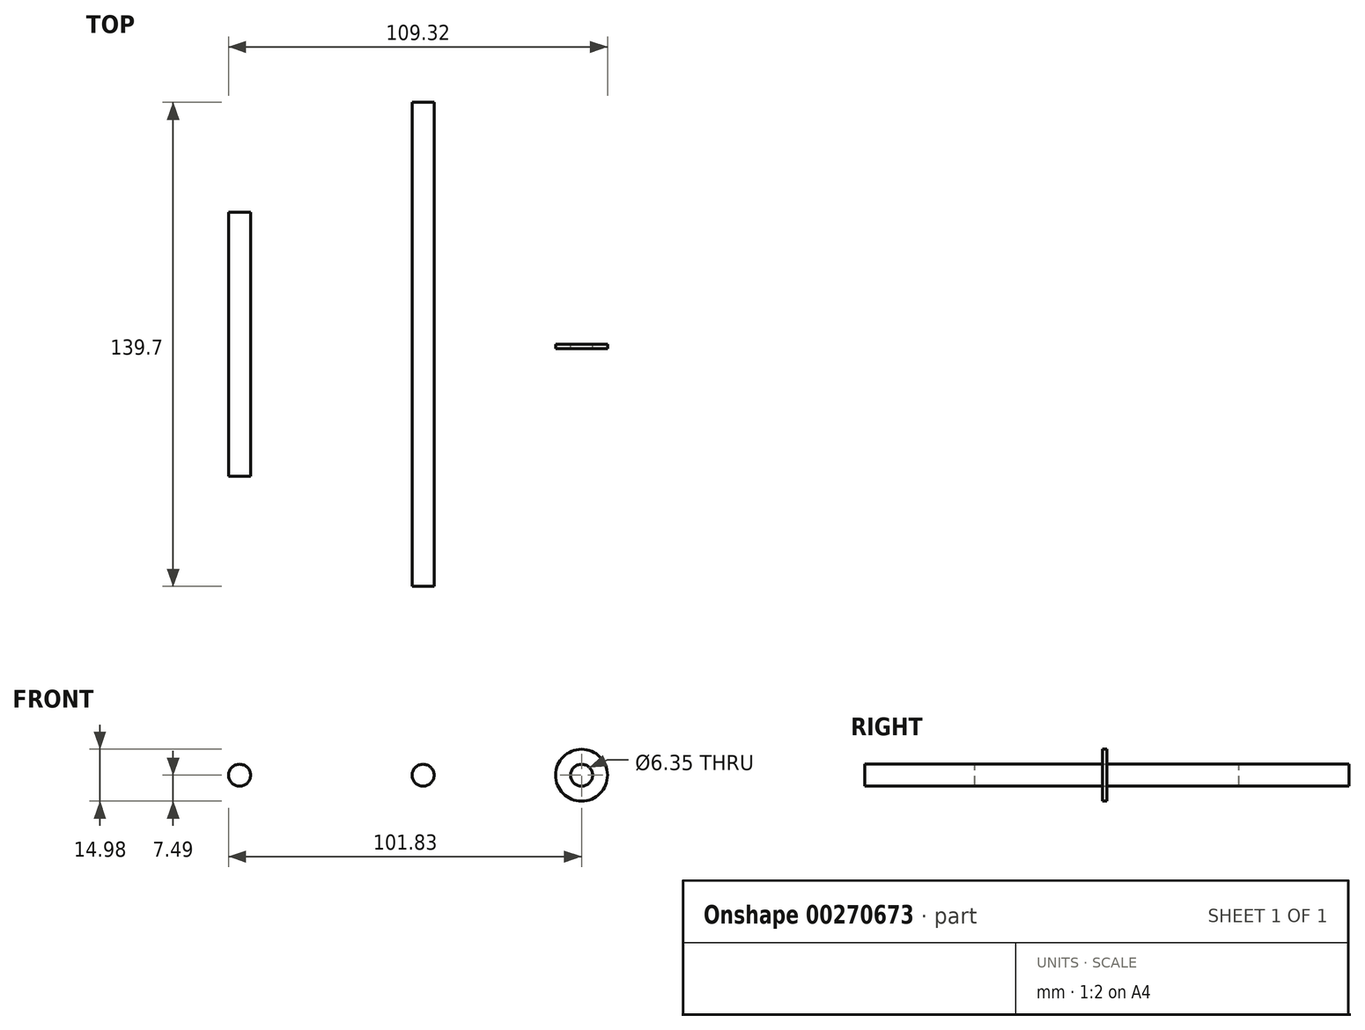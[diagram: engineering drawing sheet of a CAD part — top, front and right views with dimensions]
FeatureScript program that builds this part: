
annotation { "Feature Type Name" : "Feature", "Feature Type Description" : "" }
export const myFeature = defineFeature(function(context is Context, id is Id, definition is map)
    precondition{}
    {
        {
            var Q0;
            Q0=qCreatedBy(makeId("Front.planeOp"),FACE);
            var sketch = newSketch(context, id + "F0", { "sketchPlane" : qUnion([Q0])});
            skCircle(sketch, "E0", {"center": v(-52.94, 0) * mm, "radius": 3.18 * mm});
            skCircle(sketch, "E1", {"center": v(0, 0) * mm, "radius": 3.18 * mm});
            skSolve(sketch);
        }
        {
            var Q0;
            Q0=makeQuery(id+"F0.imprint","IMPRINT",FACE,{"disambiguationData":[TD([[makeQuery(id+"F0.imprint","IMPRINT",EDGE,{"derivedFrom":sQuery(id+"F0.wireOp",EDGE,"E0")}),1.0]])]});
            extrude(context, id + "F1", {"entities" : qUnion([Q0]), "endBound" : BoundingType.SYMMETRIC, "depth" : 76.2 * mm});
        }
        {
            var Q0;
            Q0=makeQuery(id+"F0.imprint","IMPRINT",FACE,{"disambiguationData":[TD([[makeQuery(id+"F0.imprint","IMPRINT",EDGE,{"derivedFrom":sQuery(id+"F0.wireOp",EDGE,"E1")}),1.0]])]});
            extrude(context, id + "F2", {"entities" : qUnion([Q0]), "endBound" : BoundingType.SYMMETRIC, "depth" : 139.7 * mm});
        }
        {
            var Q0;
            Q0=qCreatedBy(makeId("Front.planeOp"),FACE);
            var sketch = newSketch(context, id + "F3", { "sketchPlane" : qUnion([Q0])});
            skCircle(sketch, "E2", {"center": v(45.72, 0) * mm, "radius": 7.5 * mm});
            skCircle(sketch, "E3", {"center": v(45.72, 0) * mm, "radius": 3.18 * mm});
            skSolve(sketch);
        }
        {
            var Q0;
            Q0=makeQuery(id+"F3.imprint","IMPRINT",FACE,{"disambiguationData":[TD([[makeQuery(id+"F3.imprint","IMPRINT",EDGE,{"derivedFrom":sQuery(id+"F3.wireOp",EDGE,"E2")}),1.0]])]});
            extrude(context, id + "F4", {"entities" : qUnion([Q0]), "depth" : 1.27 * mm});
        }
    });
